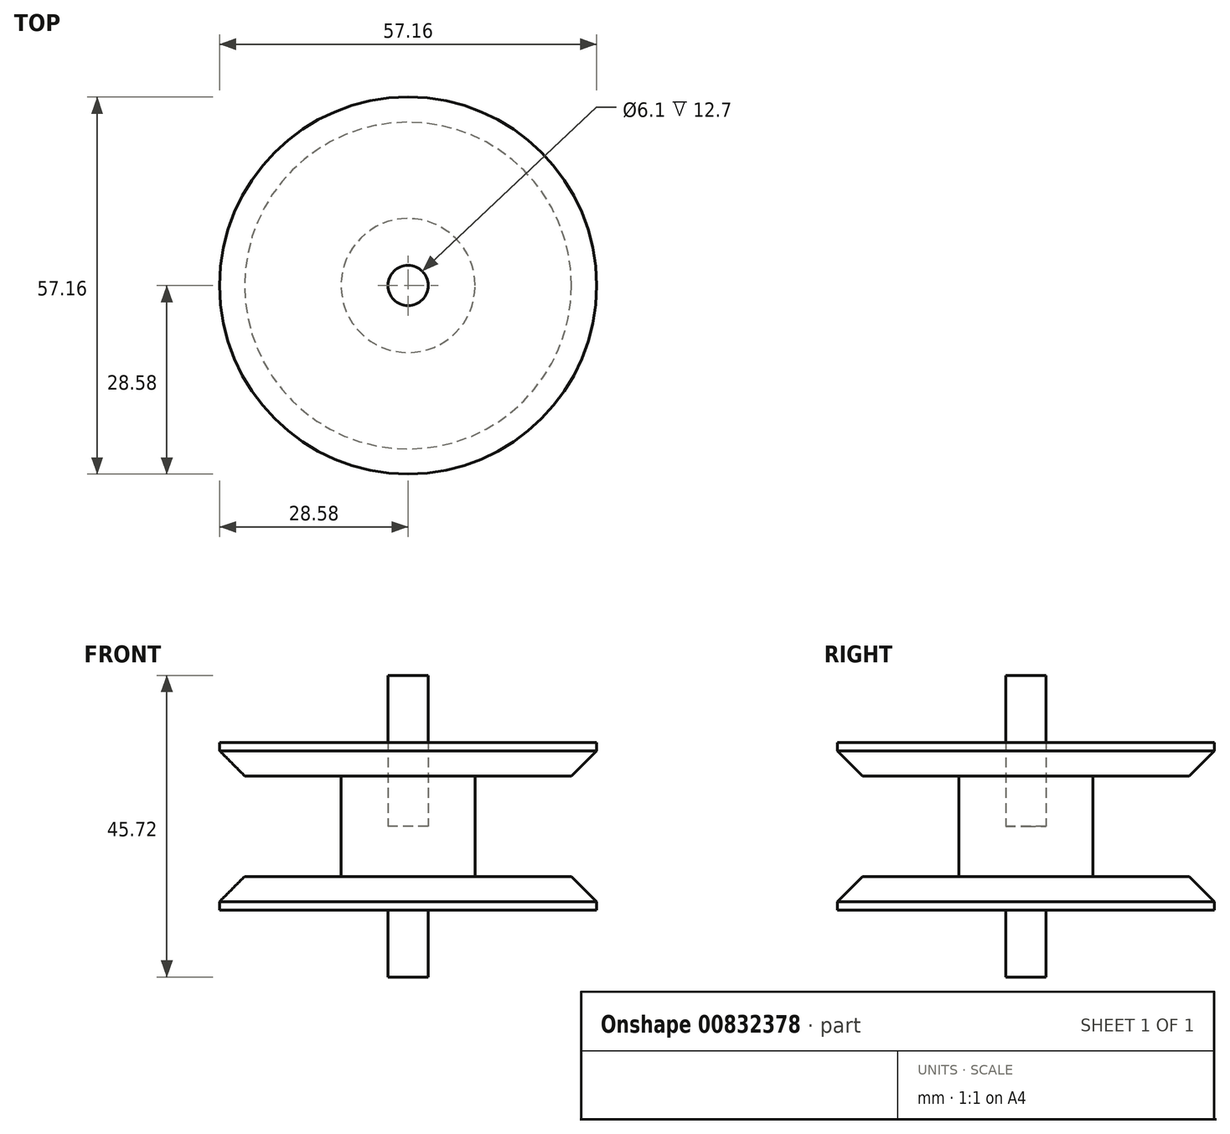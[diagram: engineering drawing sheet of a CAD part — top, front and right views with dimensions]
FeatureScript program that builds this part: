
annotation { "Feature Type Name" : "Feature", "Feature Type Description" : "" }
export const myFeature = defineFeature(function(context is Context, id is Id, definition is map)
    precondition{}
    {
        {
            var Q0;
            Q0=qCreatedBy(makeId("Top.planeOp"),FACE);
            var sketch = newSketch(context, id + "F0", { "sketchPlane" : qUnion([Q0])});
            skCircle(sketch, "E0", {"center": v(0, 0) * mm, "radius": 28.57 * mm});
            skSolve(sketch);
        }
        {
            var Q0;
            Q0=makeQuery(id+"F0.imprint","IMPRINT",FACE,{"disambiguationData":[TD([[makeQuery(id+"F0.imprint","IMPRINT",EDGE,{"derivedFrom":sQuery(id+"F0.wireOp",EDGE,"E0")}),1.0]])]});
            extrude(context, id + "F1", {"entities" : qUnion([Q0]), "depth" : 25.4 * mm, "offsetDistance" : 25.4 * mm});
        }
        {
            var Q0;
            Q0=makeQuery(id+"F1.opExtrude","CAP_FACE",FACE,{"disambiguationData":[OSD([sQuery(id+"F0.wireOp",EDGE,"E0")])],"isStart":true});
            var sketch = newSketch(context, id + "F2", { "sketchPlane" : qUnion([Q0])});
            skCircle(sketch, "E1", {"center": v(0, 0) * mm, "radius": 3.05 * mm});
            skSolve(sketch);
        }
        {
            var Q0;
            Q0=makeQuery(id+"F2.imprint","IMPRINT",FACE,{"disambiguationData":[TD([[makeQuery(id+"F2.imprint","IMPRINT",EDGE,{"derivedFrom":sQuery(id+"F2.wireOp",EDGE,"E1")}),1.0]])]});
            extrude(context, id + "F3", {"entities" : qUnion([Q0]), "operationType" : NewBodyOperationType.ADD, "depth" : 10.16 * mm, "offsetDistance" : 25.4 * mm});
        }
        {
            var Q0;
            Q0=makeQuery(id+"F1.opExtrude","CAP_FACE",FACE,{"disambiguationData":[OSD([sQuery(id+"F0.wireOp",EDGE,"E0")])],"isStart":false});
            var sketch = newSketch(context, id + "F4", { "sketchPlane" : qUnion([Q0])});
            skCircle(sketch, "E2", {"center": v(0, 0) * mm, "radius": 3.05 * mm});
            skSolve(sketch);
        }
        {
            var Q0;
            Q0=makeQuery(id+"F4.imprint","IMPRINT",FACE,{"disambiguationData":[TD([[makeQuery(id+"F4.imprint","IMPRINT",EDGE,{"derivedFrom":sQuery(id+"F4.wireOp",EDGE,"E2")}),1.0]])]});
            extrude(context, id + "F5", {"entities" : qUnion([Q0]), "operationType" : NewBodyOperationType.REMOVE, "oppositeDirection" : true, "depth" : 12.7 * mm, "offsetDistance" : 25.4 * mm});
        }
        {
            var Q0;
            Q0=makeQuery(id+"F5.boolean.opBoolean","COPY",FACE,{"derivedFrom":makeQuery(id+"F5.opExtrude","CAP_FACE",FACE,{"disambiguationData":[OSD([sQuery(id+"F4.wireOp",EDGE,"E2")])],"isStart":false})});
            extrude(context, id + "F6", {"entities" : qUnion([Q0]), "depth" : 22.86 * mm, "offsetDistance" : 25.4 * mm});
        }
        {
            var Q0;
            Q0=qCreatedBy(makeId("Right.planeOp"),FACE);
            var sketch = newSketch(context, id + "F7", { "sketchPlane" : qUnion([Q0])});
            skLineSegment(sketch, "E3.bottom", {"start": v(-34.97, 5.08) * mm, "end": v(-10.16, 5.08) * mm});
            skLineSegment(sketch, "E3.top", {"start": v(-34.97, 20.32) * mm, "end": v(-10.16, 20.32) * mm});
            skLineSegment(sketch, "E3.left", {"start": v(-34.97, 5.08) * mm, "end": v(-34.97, 20.32) * mm});
            skLineSegment(sketch, "E3.right", {"start": v(-10.16, 5.08) * mm, "end": v(-10.16, 20.32) * mm});
            skSolve(sketch);
        }
        {
            var Q0;
            Q0=makeQuery(id+"F7.imprint","IMPRINT",FACE,{"disambiguationData":[TD([[makeQuery(id+"F7.imprint","IMPRINT",EDGE,{"derivedFrom":sQuery(id+"F7.wireOp",EDGE,"E3.bottom")}),1.0]])]});
            var Q1;
            Q1=makeQuery(id+"F6.opExtrude","CAP_EDGE",EDGE,{"disambiguationData":[OSD([sQuery(id+"F4.wireOp",EDGE,"E2")])],"isStart":false});
            revolve(context, id + "F8", {"operationType" : NewBodyOperationType.REMOVE, "surfaceOperationType" : NewSurfaceOperationType.NEW, "entities" : qUnion([Q0]), "axis" : qUnion([Q1]), "revolveType" : RevolveType.FULL, "oppositeDirection" : true});
        }
        {
            var Q0;
            Q0=makeQuery(id+"F8.boolean.opBoolean","INTERSECT",EDGE,{"derivedFrom":[makeQuery(id+"F1.opExtrude","SWEPT_FACE",FACE,{"disambiguationData":[OSD([sQuery(id+"F0.wireOp",EDGE,"E0")])]}),makeQuery(id+"F8.opRevolve","SWEPT_FACE",FACE,{"disambiguationData":[OSD([sQuery(id+"F7.wireOp",EDGE,"E3.top")])]})]});
            var Q1;
            Q1=makeQuery(id+"F8.boolean.opBoolean","INTERSECT",EDGE,{"derivedFrom":[makeQuery(id+"F1.opExtrude","SWEPT_FACE",FACE,{"disambiguationData":[OSD([sQuery(id+"F0.wireOp",EDGE,"E0")])]}),makeQuery(id+"F8.opRevolve","SWEPT_FACE",FACE,{"disambiguationData":[OSD([sQuery(id+"F7.wireOp",EDGE,"E3.bottom")])]})]});
            chamfer(context, id + "F9", {"entities" : qUnion([Q0, Q1]), "width" : 3.8 * mm, "tangentPropagation" : true});
        }
    });
